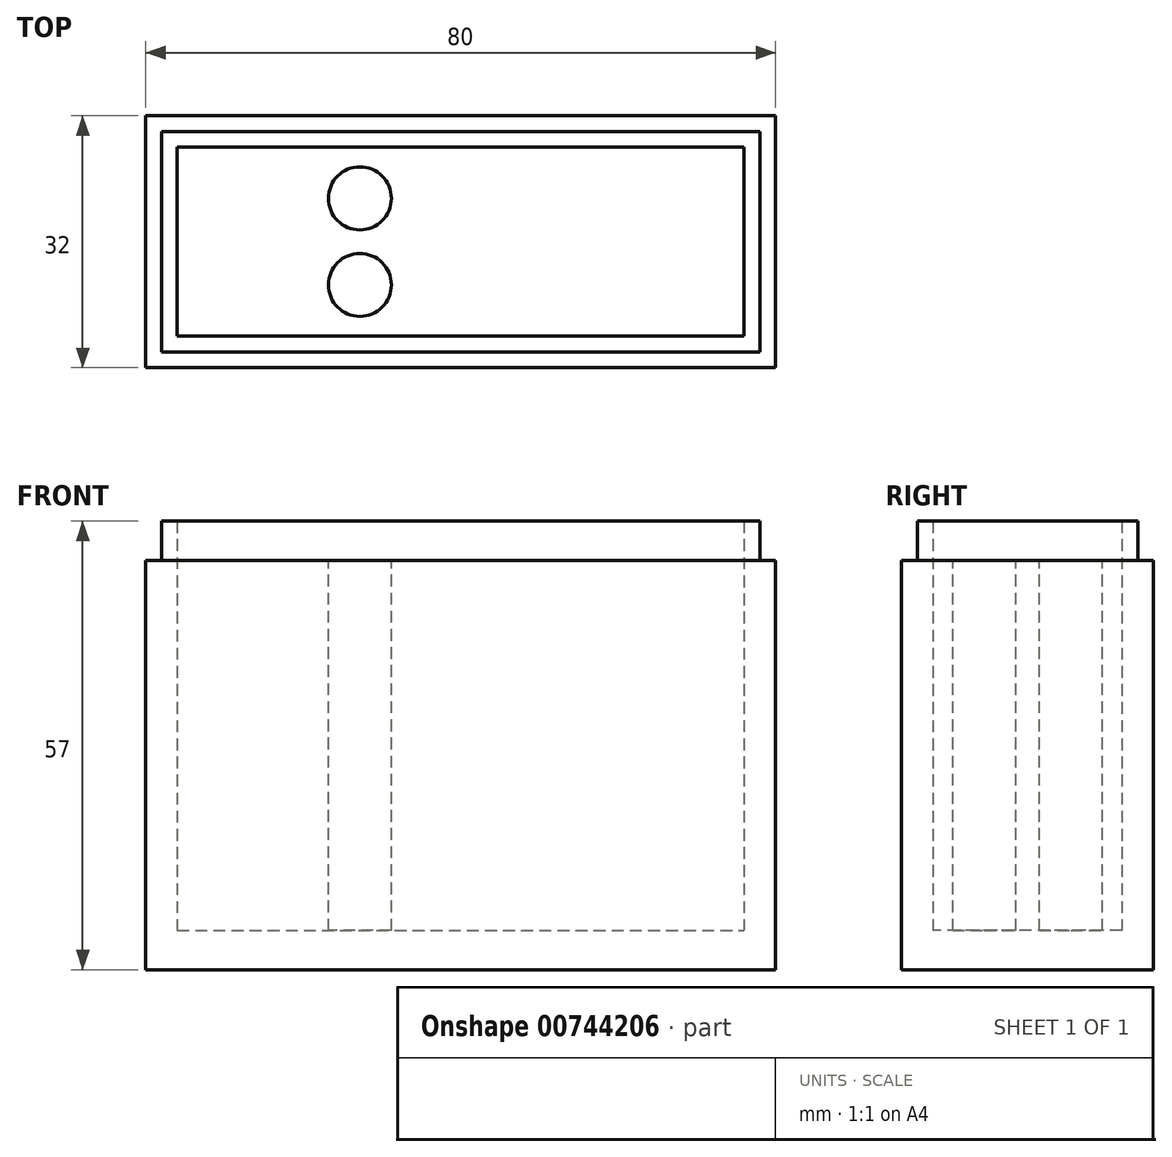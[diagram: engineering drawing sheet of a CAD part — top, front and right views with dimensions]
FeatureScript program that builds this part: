
annotation { "Feature Type Name" : "Feature", "Feature Type Description" : "" }
export const myFeature = defineFeature(function(context is Context, id is Id, definition is map)
    precondition{}
    {
        {
            var Q0;
            Q0=qCreatedBy(makeId("Top.planeOp"),FACE);
            var sketch = newSketch(context, id + "F0", { "sketchPlane" : qUnion([Q0])});
            skLineSegment(sketch, "E0.bottom", {"start": v(-53.38, 16.57) * mm, "end": v(26.62, 16.57) * mm});
            skLineSegment(sketch, "E0.top", {"start": v(-53.38, -15.43) * mm, "end": v(26.62, -15.43) * mm});
            skLineSegment(sketch, "E0.left", {"start": v(-53.38, 16.57) * mm, "end": v(-53.38, -15.43) * mm});
            skLineSegment(sketch, "E0.right", {"start": v(26.62, 16.57) * mm, "end": v(26.62, -15.43) * mm});
            skLineSegment(sketch, "E1.bottom", {"start": v(-51.38, 14.57) * mm, "end": v(24.62, 14.57) * mm});
            skLineSegment(sketch, "E1.top", {"start": v(-51.38, -13.43) * mm, "end": v(24.62, -13.43) * mm});
            skLineSegment(sketch, "E1.left", {"start": v(-51.38, 14.57) * mm, "end": v(-51.38, -13.43) * mm});
            skLineSegment(sketch, "E1.right", {"start": v(24.62, 14.57) * mm, "end": v(24.62, -13.43) * mm});
            skLineSegment(sketch, "E2.bottom", {"start": v(-49.38, 12.57) * mm, "end": v(22.62, 12.57) * mm});
            skLineSegment(sketch, "E2.top", {"start": v(-49.38, -11.43) * mm, "end": v(22.62, -11.43) * mm});
            skLineSegment(sketch, "E2.left", {"start": v(-49.38, 12.57) * mm, "end": v(-49.38, -11.43) * mm});
            skLineSegment(sketch, "E2.right", {"start": v(22.62, 12.57) * mm, "end": v(22.62, -11.43) * mm});
            skSolve(sketch);
        }
        {
            var Q0;
            Q0=makeQuery(id+"F0.imprint","IMPRINT",FACE,{"disambiguationData":[TD([[makeQuery(id+"F0.imprint","IMPRINT",EDGE,{"derivedFrom":sQuery(id+"F0.wireOp",EDGE,"E0.bottom")}),-1.0]])]});
            extrude(context, id + "F1", {"entities" : qUnion([Q0]), "depth" : 52 * mm, "offsetDistance" : 25 * mm});
        }
        {
            var Q0;
            Q0=makeQuery(id+"F0.imprint","IMPRINT",FACE,{"disambiguationData":[TD([[makeQuery(id+"F0.imprint","IMPRINT",EDGE,{"derivedFrom":sQuery(id+"F0.wireOp",EDGE,"E1.bottom")}),-1.0]])]});
            extrude(context, id + "F2", {"entities" : qUnion([Q0]), "operationType" : NewBodyOperationType.ADD, "depth" : 57 * mm, "offsetDistance" : 25 * mm});
        }
        {
            var Q0;
            Q0=makeQuery(id+"F0.imprint","IMPRINT",FACE,{"disambiguationData":[TD([[makeQuery(id+"F0.imprint","IMPRINT",EDGE,{"derivedFrom":sQuery(id+"F0.wireOp",EDGE,"E2.bottom")}),-1.0]])]});
            extrude(context, id + "F3", {"entities" : qUnion([Q0]), "operationType" : NewBodyOperationType.ADD, "depth" : 52 * mm, "offsetDistance" : 25 * mm});
        }
        {
            var Q0;
            Q0=makeQuery(id+"F3.opExtrude","CAP_FACE",FACE,{"disambiguationData":[OSD([sQuery(id+"F0.wireOp",EDGE,"E2.bottom"),sQuery(id+"F0.wireOp",EDGE,"E2.top"),sQuery(id+"F0.wireOp",EDGE,"E2.left"),sQuery(id+"F0.wireOp",EDGE,"E2.right")])],"isStart":false});
            var sketch = newSketch(context, id + "F4", { "sketchPlane" : qUnion([Q0])});
            skCircle(sketch, "E3", {"center": v(-42.88, -4.93) * mm, "radius": 4 * mm});
            skCircle(sketch, "E4", {"center": v(-42.88, 6.07) * mm, "radius": 4 * mm});
            skCircle(sketch, "E5", {"center": v(-34.53, 0.57) * mm, "radius": 4 * mm});
            skCircle(sketch, "E6.MirrorC", {"center": v(-26.18, -4.93) * mm, "radius": 4 * mm});
            skCircle(sketch, "E7.MirrorC", {"center": v(-26.18, 6.07) * mm, "radius": 4 * mm});
            skLineSegment(sketch, "E8.bottom", {"start": v(8.53, 11.75) * mm, "end": v(20.38, 11.75) * mm});
            skLineSegment(sketch, "E8.top", {"start": v(8.53, -10.25) * mm, "end": v(20.38, -10.25) * mm});
            skLineSegment(sketch, "E8.left", {"start": v(8.53, 11.75) * mm, "end": v(8.53, -10.25) * mm});
            skLineSegment(sketch, "E8.right", {"start": v(20.38, 11.75) * mm, "end": v(20.38, -10.25) * mm});
            skSolve(sketch);
        }
        {
            var Q0;
            Q0=makeQuery(id+"F4.imprint","IMPRINT",FACE,{"disambiguationData":[TD([[makeQuery(id+"F4.imprint","IMPRINT",EDGE,{"derivedFrom":sQuery(id+"F4.wireOp",EDGE,"E3")}),1.0]])]});
            var Q1;
            Q1=makeQuery(id+"F4.imprint","IMPRINT",FACE,{"disambiguationData":[TD([[makeQuery(id+"F4.imprint","IMPRINT",EDGE,{"derivedFrom":sQuery(id+"F4.wireOp",EDGE,"E5")}),1.0]])]});
            var Q2;
            Q2=makeQuery(id+"F4.imprint","IMPRINT",FACE,{"disambiguationData":[TD([[makeQuery(id+"F4.imprint","IMPRINT",EDGE,{"derivedFrom":sQuery(id+"F4.wireOp",EDGE,"E6.MirrorC")}),-1.0]])]});
            var Q3;
            Q3=makeQuery(id+"F4.imprint","IMPRINT",FACE,{"disambiguationData":[TD([[makeQuery(id+"F4.imprint","IMPRINT",EDGE,{"derivedFrom":sQuery(id+"F4.wireOp",EDGE,"E7.MirrorC")}),-1.0]])]});
            var Q4;
            Q4=makeQuery(id+"F4.imprint","IMPRINT",FACE,{"disambiguationData":[TD([[makeQuery(id+"F4.imprint","IMPRINT",EDGE,{"derivedFrom":sQuery(id+"F4.wireOp",EDGE,"E4")}),1.0]])]});
            var Q5;
            Q5=makeQuery(id+"F4.imprint","IMPRINT",FACE,{"disambiguationData":[TD([[makeQuery(id+"F4.imprint","IMPRINT",EDGE,{"derivedFrom":sQuery(id+"F4.wireOp",EDGE,"E8.bottom")}),-1.0]])]});
            extrude(context, id + "F5", {"entities" : qUnion([Q0, Q1, Q2, Q3, Q4, Q5]), "operationType" : NewBodyOperationType.REMOVE, "oppositeDirection" : true, "depth" : 47 * mm, "offsetDistance" : 25 * mm});
        }
    });
